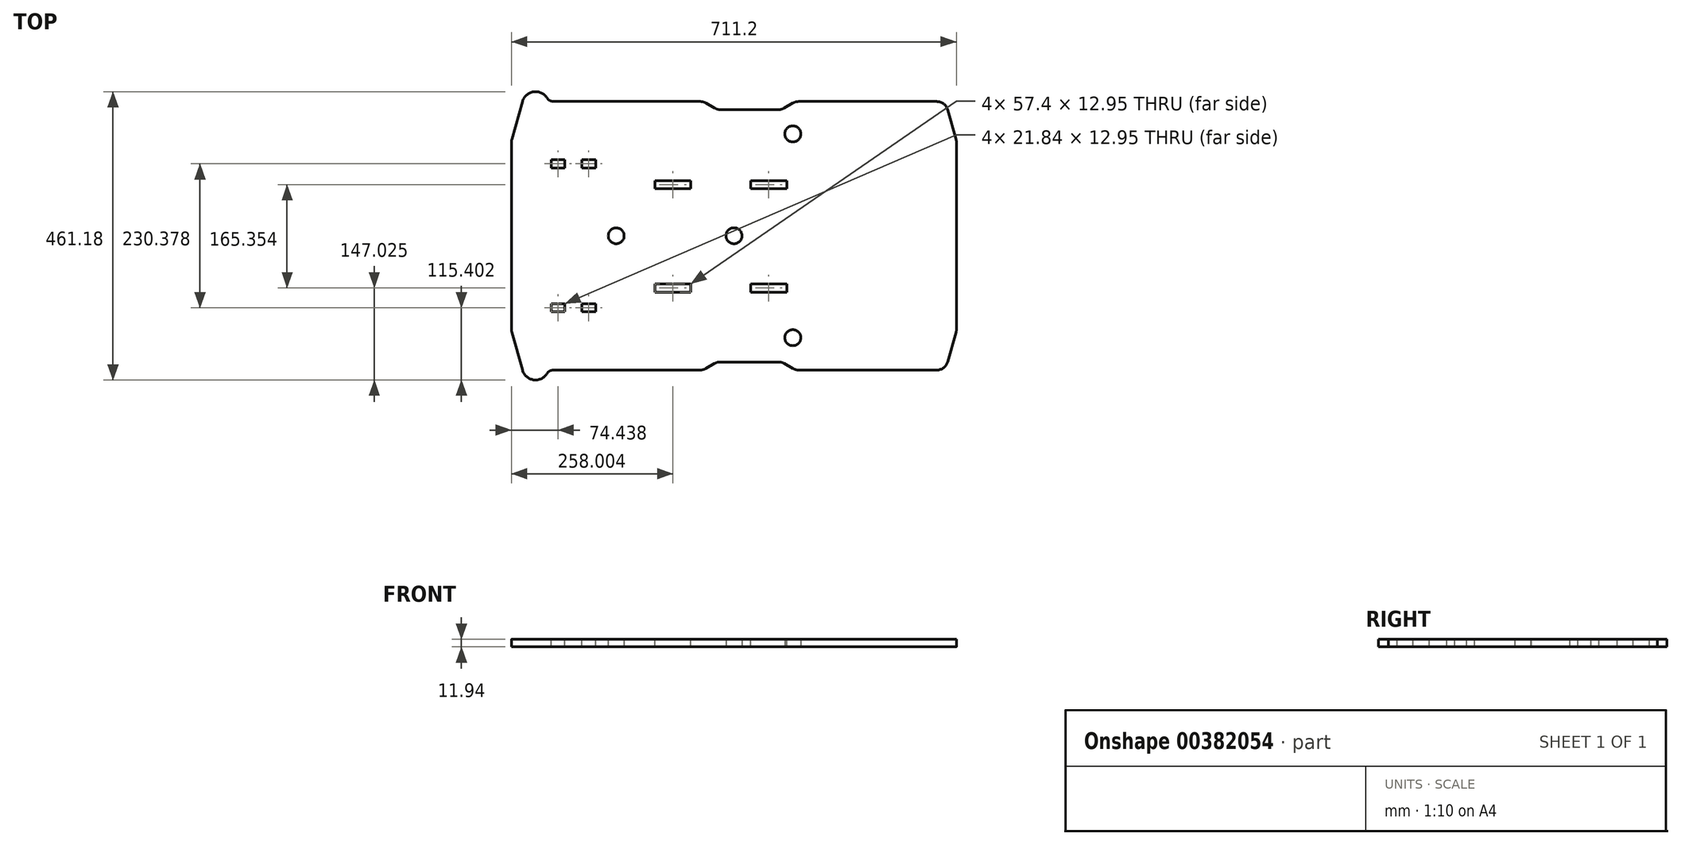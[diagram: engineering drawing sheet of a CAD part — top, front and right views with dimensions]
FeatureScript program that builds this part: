
annotation { "Feature Type Name" : "Feature", "Feature Type Description" : "" }
export const myFeature = defineFeature(function(context is Context, id is Id, definition is map)
    precondition{}
    {
        {
            var Q0;
            Q0=qCreatedBy(makeId("Top.planeOp"),FACE);
            var sketch = newSketch(context, id + "F0", { "sketchPlane" : qUnion([Q0])});
            skLineSegment(sketch, "E0.0", {"start": v(72.27, -53.52) * mm, "end": v(58.34, -61.56) * mm});
            skLineSegment(sketch, "E1.MirrorCS", {"start": v(72.27, 355.04) * mm, "end": v(58.34, 363.08) * mm});
            skLineSegment(sketch, "E2", {"start": v(81.54, -51.03) * mm, "end": v(174.21, -51.03) * mm});
            skLineSegment(sketch, "E3", {"start": v(81.54, 352.55) * mm, "end": v(174.21, 352.55) * mm});
            skLineSegment(sketch, "E4", {"start": v(49.07, 365.56) * mm, "end": v(-185.33, 365.56) * mm});
            skLineSegment(sketch, "E5", {"start": v(49.07, -64.04) * mm, "end": v(-185.33, -64.04) * mm});
            skArc(sketch, "E6", {"start": v(-234.87, -64.04) * mm, "mid": v(-217.19, -79.6) * mm, "end": v(-195.77, -69.78) * mm});
            skPoint(sketch, "E7.visualSharp", {"position": v(-193.21, -64.04) * mm});
            skArc(sketch, "E7.filletArc", {"start": v(-185.33, -64.04) * mm, "mid": v(-191.29, -65.57) * mm, "end": v(-195.77, -69.78) * mm});
            skLineSegment(sketch, "E8", {"start": v(-234.87, -64.04) * mm, "end": v(-251.8, -3.7) * mm});
            skArc(sketch, "E9.MirrorCS", {"start": v(-185.33, 365.56) * mm, "mid": v(-191.29, 367.1) * mm, "end": v(-195.77, 371.3) * mm});
            skArc(sketch, "E10.MirrorCS", {"start": v(-234.87, 365.56) * mm, "mid": v(-217.19, 381.12) * mm, "end": v(-195.77, 371.3) * mm});
            skLineSegment(sketch, "E11", {"start": v(-234.87, 365.56) * mm, "end": v(-251.8, 305.22) * mm});
            skLineSegment(sketch, "E12", {"start": v(-252.5, 19.7) * mm, "end": v(-252.5, 1.31) * mm});
            skLineSegment(sketch, "E13", {"start": v(-252.5, 281.82) * mm, "end": v(-252.5, 300.2) * mm});
            skPoint(sketch, "E14.visualSharp", {"position": v(-252.5, -1.24) * mm});
            skArc(sketch, "E14.filletArc", {"start": v(-252.5, 1.31) * mm, "mid": v(-252.32, -1.21) * mm, "end": v(-251.8, -3.7) * mm});
            skPoint(sketch, "E15.visualSharp", {"position": v(-252.5, 302.76) * mm});
            skArc(sketch, "E15.filletArc", {"start": v(-251.8, 305.22) * mm, "mid": v(-252.32, 302.74) * mm, "end": v(-252.5, 300.2) * mm});
            skLineSegment(sketch, "E16.MirrorCS", {"start": v(183.48, 355.04) * mm, "end": v(197.4, 363.08) * mm});
            skLineSegment(sketch, "E17.MirrorCS", {"start": v(183.48, -53.52) * mm, "end": v(197.4, -61.56) * mm});
            skLineSegment(sketch, "E18.MirrorCS", {"start": v(444.88, -50.5) * mm, "end": v(458.01, -3.7) * mm});
            skArc(sketch, "E19.MirrorCS", {"start": v(458.7, 1.31) * mm, "mid": v(458.53, -1.21) * mm, "end": v(458.01, -3.7) * mm});
            skLineSegment(sketch, "E20.MirrorCS", {"start": v(458.7, 19.7) * mm, "end": v(458.7, 1.31) * mm});
            skLineSegment(sketch, "E21.MirrorCS", {"start": v(458.7, 281.82) * mm, "end": v(458.7, 300.2) * mm});
            skArc(sketch, "E22.MirrorCS", {"start": v(458.01, 305.22) * mm, "mid": v(458.53, 302.74) * mm, "end": v(458.7, 300.2) * mm});
            skLineSegment(sketch, "E23.MirrorCS", {"start": v(444.88, 352.03) * mm, "end": v(458.01, 305.22) * mm});
            skLineSegment(sketch, "E24.MirrorCS", {"start": v(206.68, -64.04) * mm, "end": v(427.02, -64.04) * mm});
            skLineSegment(sketch, "E25.MirrorCS", {"start": v(206.68, 365.56) * mm, "end": v(427.02, 365.56) * mm});
            skPoint(sketch, "E26.visualSharp", {"position": v(441.08, 365.56) * mm});
            skArc(sketch, "E26.filletArc", {"start": v(444.88, 352.03) * mm, "mid": v(438.23, 361.8) * mm, "end": v(427.02, 365.56) * mm});
            skPoint(sketch, "E27.visualSharp", {"position": v(441.08, -64.04) * mm});
            skArc(sketch, "E27.filletArc", {"start": v(427.02, -64.04) * mm, "mid": v(438.23, -60.27) * mm, "end": v(444.88, -50.5) * mm});
            skPoint(sketch, "E28.visualSharp", {"position": v(54.04, -64.04) * mm});
            skArc(sketch, "E28.filletArc", {"start": v(49.07, -64.04) * mm, "mid": v(53.87, -63.4) * mm, "end": v(58.34, -61.56) * mm});
            skPoint(sketch, "E29.visualSharp", {"position": v(76.57, -51.03) * mm});
            skArc(sketch, "E29.filletArc", {"start": v(81.54, -51.03) * mm, "mid": v(76.74, -51.67) * mm, "end": v(72.27, -53.52) * mm});
            skPoint(sketch, "E30.visualSharp", {"position": v(179.18, -51.03) * mm});
            skArc(sketch, "E30.filletArc", {"start": v(183.48, -53.52) * mm, "mid": v(179.01, -51.67) * mm, "end": v(174.21, -51.03) * mm});
            skPoint(sketch, "E31.visualSharp", {"position": v(201.7, -64.04) * mm});
            skArc(sketch, "E31.filletArc", {"start": v(197.4, -61.56) * mm, "mid": v(201.88, -63.4) * mm, "end": v(206.68, -64.04) * mm});
            skPoint(sketch, "E32.visualSharp", {"position": v(179.18, 352.55) * mm});
            skArc(sketch, "E32.filletArc", {"start": v(174.21, 352.55) * mm, "mid": v(179.01, 353.19) * mm, "end": v(183.48, 355.04) * mm});
            skPoint(sketch, "E33.visualSharp", {"position": v(201.7, 365.56) * mm});
            skArc(sketch, "E33.filletArc", {"start": v(206.68, 365.56) * mm, "mid": v(201.88, 364.93) * mm, "end": v(197.4, 363.08) * mm});
            skPoint(sketch, "E34.visualSharp", {"position": v(76.57, 352.55) * mm});
            skArc(sketch, "E34.filletArc", {"start": v(72.27, 355.04) * mm, "mid": v(76.74, 353.19) * mm, "end": v(81.54, 352.55) * mm});
            skPoint(sketch, "E35.visualSharp", {"position": v(54.04, 365.56) * mm});
            skArc(sketch, "E35.filletArc", {"start": v(58.34, 363.08) * mm, "mid": v(53.87, 364.93) * mm, "end": v(49.07, 365.56) * mm});
            skLineSegment(sketch, "E36", {"start": v(-252.5, 281.82) * mm, "end": v(-252.5, 19.7) * mm});
            skLineSegment(sketch, "E37", {"start": v(458.7, 281.82) * mm, "end": v(458.7, 19.7) * mm});
            skCircle(sketch, "E38", {"center": v(103.1, 150.76) * mm, "radius": 12.83 * mm});
            skLineSegment(sketch, "E39", {"start": v(103.31, 163.59) * mm, "end": v(103.31, 352.55) * mm, "construction": true});
            skCircle(sketch, "E40", {"center": v(-85.09, 150.76) * mm, "radius": 12.7 * mm});
            skPoint(sketch, "E41", {"position": v(197.2, -12.22) * mm});
            skPoint(sketch, "E42", {"position": v(197.2, 313.74) * mm});
            skCircle(sketch, "E43", {"center": v(197.2, -12.22) * mm, "radius": 12.83 * mm});
            skCircle(sketch, "E44", {"center": v(197.2, 313.74) * mm, "radius": 12.83 * mm});
            skSolve(sketch);
        }
        {
            var Q0;
            Q0=makeQuery(id+"F0.imprint","IMPRINT",FACE,{"disambiguationData":[TD([[makeQuery(id+"F0.imprint","IMPRINT",EDGE,{"derivedFrom":sQuery(id+"F0.wireOp",EDGE,"E0.0")}),-1.0]])]});
            extrude(context, id + "F1", {"entities" : qUnion([Q0]), "depth" : 11.94 * mm});
        }
        {
            var Q0;
            Q0=makeQuery(id+"F1.opExtrude","CAP_FACE",FACE,{"disambiguationData":[OSD([sQuery(id+"F0.wireOp",EDGE,"E0.0"),sQuery(id+"F0.wireOp",EDGE,"E1.MirrorCS"),sQuery(id+"F0.wireOp",EDGE,"E2"),sQuery(id+"F0.wireOp",EDGE,"E3"),sQuery(id+"F0.wireOp",EDGE,"E4"),sQuery(id+"F0.wireOp",EDGE,"E5"),sQuery(id+"F0.wireOp",EDGE,"E6"),sQuery(id+"F0.wireOp",EDGE,"E7.filletArc"),sQuery(id+"F0.wireOp",EDGE,"E8"),sQuery(id+"F0.wireOp",EDGE,"E9.MirrorCS"),sQuery(id+"F0.wireOp",EDGE,"E10.MirrorCS"),sQuery(id+"F0.wireOp",EDGE,"E11"),sQuery(id+"F0.wireOp",EDGE,"E12"),sQuery(id+"F0.wireOp",EDGE,"E13"),sQuery(id+"F0.wireOp",EDGE,"E14.filletArc"),sQuery(id+"F0.wireOp",EDGE,"E15.filletArc"),sQuery(id+"F0.wireOp",EDGE,"E16.MirrorCS"),sQuery(id+"F0.wireOp",EDGE,"E17.MirrorCS"),sQuery(id+"F0.wireOp",EDGE,"E18.MirrorCS"),sQuery(id+"F0.wireOp",EDGE,"E19.MirrorCS"),sQuery(id+"F0.wireOp",EDGE,"E20.MirrorCS"),sQuery(id+"F0.wireOp",EDGE,"E21.MirrorCS"),sQuery(id+"F0.wireOp",EDGE,"E22.MirrorCS"),sQuery(id+"F0.wireOp",EDGE,"E23.MirrorCS"),sQuery(id+"F0.wireOp",EDGE,"E24.MirrorCS"),sQuery(id+"F0.wireOp",EDGE,"E25.MirrorCS"),sQuery(id+"F0.wireOp",EDGE,"E26.filletArc"),sQuery(id+"F0.wireOp",EDGE,"E27.filletArc"),sQuery(id+"F0.wireOp",EDGE,"E28.filletArc"),sQuery(id+"F0.wireOp",EDGE,"E29.filletArc"),sQuery(id+"F0.wireOp",EDGE,"E30.filletArc"),sQuery(id+"F0.wireOp",EDGE,"E31.filletArc"),sQuery(id+"F0.wireOp",EDGE,"E32.filletArc"),sQuery(id+"F0.wireOp",EDGE,"E33.filletArc"),sQuery(id+"F0.wireOp",EDGE,"E34.filletArc"),sQuery(id+"F0.wireOp",EDGE,"E35.filletArc"),sQuery(id+"F0.wireOp",EDGE,"E36"),sQuery(id+"F0.wireOp",EDGE,"E37"),sQuery(id+"F0.wireOp",EDGE,"E38"),sQuery(id+"F0.wireOp",EDGE,"E40"),sQuery(id+"F0.wireOp",EDGE,"E43"),sQuery(id+"F0.wireOp",EDGE,"E44")])],"isStart":false});
            var sketch = newSketch(context, id + "F2", { "sketchPlane" : qUnion([Q0])});
            skLineSegment(sketch, "E45", {"start": v(-185.8, 29.1) * mm, "end": v(-170.31, 29.1) * mm});
            skLineSegment(sketch, "E46", {"start": v(-185.8, 42.05) * mm, "end": v(-170.31, 42.05) * mm});
            skLineSegment(sketch, "E47", {"start": v(-170.31, 35.57) * mm, "end": v(-136.6, 35.57) * mm, "construction": true});
            skLineSegment(sketch, "E48", {"start": v(-153.46, 35.57) * mm, "end": v(-153.46, 41.61) * mm, "construction": true});
            skLineSegment(sketch, "E49.MirrorCS", {"start": v(-136.6, 29.1) * mm, "end": v(-136.6, 42.05) * mm, "construction": true});
            skLineSegment(sketch, "E50.MirrorCS", {"start": v(-121.11, 42.05) * mm, "end": v(-136.6, 42.05) * mm});
            skLineSegment(sketch, "E51.MirrorCS", {"start": v(-139.78, 35.57) * mm, "end": v(-170.31, 35.57) * mm, "construction": true});
            skLineSegment(sketch, "E52.MirrorCS", {"start": v(-121.11, 29.1) * mm, "end": v(-121.11, 42.05) * mm, "construction": true});
            skLineSegment(sketch, "E53.MirrorCS", {"start": v(-121.11, 29.1) * mm, "end": v(-136.6, 29.1) * mm});
            skLineSegment(sketch, "E54", {"start": v(-185.8, 42.05) * mm, "end": v(-185.8, 259.47) * mm, "construction": true});
            skLineSegment(sketch, "E55", {"start": v(-185.8, 150.76) * mm, "end": v(-157.57, 150.76) * mm, "construction": true});
            skLineSegment(sketch, "E56.MirrorCS", {"start": v(-170.31, 265.95) * mm, "end": v(-136.6, 265.95) * mm, "construction": true});
            skLineSegment(sketch, "E57.MirrorCS", {"start": v(-153.46, 265.95) * mm, "end": v(-153.46, 259.9) * mm, "construction": true});
            skLineSegment(sketch, "E58.MirrorCS", {"start": v(-121.11, 259.47) * mm, "end": v(-136.6, 259.47) * mm});
            skLineSegment(sketch, "E59.MirrorCS", {"start": v(-136.6, 265.95) * mm, "end": v(-170.31, 265.95) * mm, "construction": true});
            skLineSegment(sketch, "E60.MirrorCS", {"start": v(-185.8, 272.43) * mm, "end": v(-170.31, 272.43) * mm});
            skLineSegment(sketch, "E61.MirrorCS", {"start": v(-121.11, 272.43) * mm, "end": v(-136.6, 272.43) * mm});
            skLineSegment(sketch, "E62.MirrorCS", {"start": v(-185.8, 259.47) * mm, "end": v(-170.31, 259.47) * mm});
            skLineSegment(sketch, "E63", {"start": v(-178.06, 29.1) * mm, "end": v(-178.06, 42.05) * mm, "construction": true});
            skLineSegment(sketch, "E64", {"start": v(-128.86, 29.1) * mm, "end": v(-128.86, 42.05) * mm, "construction": true});
            skLineSegment(sketch, "E65", {"start": v(-121.11, 42.05) * mm, "end": v(-117.94, 42.05) * mm});
            skLineSegment(sketch, "E66", {"start": v(-117.94, 42.05) * mm, "end": v(-117.94, 29.1) * mm});
            skLineSegment(sketch, "E67", {"start": v(-121.11, 29.1) * mm, "end": v(-117.94, 29.1) * mm});
            skLineSegment(sketch, "E68.MirrorCS", {"start": v(-136.6, 42.05) * mm, "end": v(-139.78, 42.05) * mm});
            skLineSegment(sketch, "E69.MirrorCS", {"start": v(-139.78, 42.05) * mm, "end": v(-139.78, 29.1) * mm});
            skLineSegment(sketch, "E70.MirrorCS", {"start": v(-136.6, 29.1) * mm, "end": v(-139.78, 29.1) * mm});
            skPoint(sketch, "E71.orphan", {"position": v(-136.6, 35.57) * mm});
            skLineSegment(sketch, "E72", {"start": v(-170.31, 42.05) * mm, "end": v(-167.14, 42.05) * mm});
            skLineSegment(sketch, "E73", {"start": v(-167.14, 42.05) * mm, "end": v(-167.14, 29.1) * mm});
            skLineSegment(sketch, "E74", {"start": v(-170.31, 29.1) * mm, "end": v(-167.14, 29.1) * mm});
            skLineSegment(sketch, "E75.MirrorCS", {"start": v(-185.8, 42.05) * mm, "end": v(-188.98, 42.05) * mm});
            skLineSegment(sketch, "E76.MirrorCS", {"start": v(-188.98, 42.05) * mm, "end": v(-188.98, 29.1) * mm});
            skLineSegment(sketch, "E77.MirrorCS", {"start": v(-185.8, 29.1) * mm, "end": v(-188.98, 29.1) * mm});
            skPoint(sketch, "E78", {"position": v(-170.31, 42.05) * mm});
            skPoint(sketch, "E79", {"position": v(-170.31, 29.1) * mm});
            skLineSegment(sketch, "E80", {"start": v(-170.31, 29.1) * mm, "end": v(-170.31, 42.05) * mm, "construction": true});
            skPoint(sketch, "E81", {"position": v(-185.8, 42.05) * mm});
            skPoint(sketch, "E82", {"position": v(-185.8, 29.1) * mm});
            skLineSegment(sketch, "E83", {"start": v(-185.8, 29.1) * mm, "end": v(-185.8, 42.05) * mm, "construction": true});
            skLineSegment(sketch, "E84.MirrorCS", {"start": v(-185.8, 259.47) * mm, "end": v(-188.98, 259.47) * mm});
            skLineSegment(sketch, "E85.MirrorCS", {"start": v(-170.31, 272.43) * mm, "end": v(-167.14, 272.43) * mm});
            skLineSegment(sketch, "E86.MirrorCS", {"start": v(-170.31, 259.47) * mm, "end": v(-167.14, 259.47) * mm});
            skLineSegment(sketch, "E87.MirrorCS", {"start": v(-188.98, 259.47) * mm, "end": v(-188.98, 272.43) * mm});
            skLineSegment(sketch, "E88.MirrorCS", {"start": v(-167.14, 259.47) * mm, "end": v(-167.14, 272.43) * mm});
            skLineSegment(sketch, "E89.MirrorCS", {"start": v(-136.6, 272.43) * mm, "end": v(-139.78, 272.43) * mm});
            skLineSegment(sketch, "E90.MirrorCS", {"start": v(-185.8, 272.43) * mm, "end": v(-188.98, 272.43) * mm});
            skLineSegment(sketch, "E91.MirrorCS", {"start": v(-121.11, 259.47) * mm, "end": v(-117.94, 259.47) * mm});
            skLineSegment(sketch, "E92.MirrorCS", {"start": v(-117.94, 259.47) * mm, "end": v(-117.94, 272.43) * mm});
            skLineSegment(sketch, "E93.MirrorCS", {"start": v(-121.11, 272.43) * mm, "end": v(-117.94, 272.43) * mm});
            skLineSegment(sketch, "E94.MirrorCS", {"start": v(-136.6, 259.47) * mm, "end": v(-139.78, 259.47) * mm});
            skLineSegment(sketch, "E95.MirrorCS", {"start": v(-139.78, 259.47) * mm, "end": v(-139.78, 272.43) * mm});
            skLineSegment(sketch, "E96.MirrorCS", {"start": v(-178.06, 272.43) * mm, "end": v(-178.06, 259.47) * mm, "construction": true});
            skLineSegment(sketch, "E97.MirrorCS", {"start": v(-128.86, 272.43) * mm, "end": v(-128.86, 259.47) * mm, "construction": true});
            skLineSegment(sketch, "E98.MirrorCS", {"start": v(-139.78, 265.95) * mm, "end": v(-170.31, 265.95) * mm, "construction": true});
            skPoint(sketch, "E99.MirrorP", {"position": v(-170.31, 259.47) * mm});
            skPoint(sketch, "E100.MirrorP", {"position": v(-170.31, 272.43) * mm});
            skPoint(sketch, "E101.MirrorP", {"position": v(-185.8, 272.43) * mm});
            skPoint(sketch, "E102.MirrorP", {"position": v(-136.6, 265.95) * mm});
            skPoint(sketch, "E103.MirrorP", {"position": v(-185.8, 259.47) * mm});
            skLineSegment(sketch, "E104", {"start": v(-170.31, 259.47) * mm, "end": v(-170.31, 272.43) * mm, "construction": true});
            skLineSegment(sketch, "E105", {"start": v(-185.8, 259.47) * mm, "end": v(-185.8, 272.43) * mm, "construction": true});
            skPoint(sketch, "E106", {"position": v(-136.6, 272.43) * mm});
            skPoint(sketch, "E107", {"position": v(-121.11, 272.43) * mm});
            skPoint(sketch, "E108", {"position": v(-121.11, 259.47) * mm});
            skPoint(sketch, "E109", {"position": v(-136.6, 259.47) * mm});
            skLineSegment(sketch, "E110", {"start": v(-136.6, 259.47) * mm, "end": v(-136.6, 272.43) * mm, "construction": true});
            skLineSegment(sketch, "E111", {"start": v(-121.11, 272.43) * mm, "end": v(-121.11, 259.47) * mm, "construction": true});
            skSolve(sketch);
        }
        {
            var Q0;
            Q0=makeQuery(id+"F2.imprint","IMPRINT",FACE,{"disambiguationData":[TD([[makeQuery(id+"F2.imprint","IMPRINT",EDGE,{"derivedFrom":sQuery(id+"F2.wireOp",EDGE,"E84.MirrorCS")}),-1.0]])]});
            var Q1;
            Q1=makeQuery(id+"F2.imprint","IMPRINT",FACE,{"disambiguationData":[TD([[makeQuery(id+"F2.imprint","IMPRINT",EDGE,{"derivedFrom":sQuery(id+"F2.wireOp",EDGE,"E89.MirrorCS")}),1.0]])]});
            var Q2;
            Q2=makeQuery(id+"F2.imprint","IMPRINT",FACE,{"disambiguationData":[TD([[makeQuery(id+"F2.imprint","IMPRINT",EDGE,{"derivedFrom":sQuery(id+"F2.wireOp",EDGE,"E45")}),1.0]])]});
            var Q3;
            Q3=makeQuery(id+"F2.imprint","IMPRINT",FACE,{"disambiguationData":[TD([[makeQuery(id+"F2.imprint","IMPRINT",EDGE,{"derivedFrom":sQuery(id+"F2.wireOp",EDGE,"E50.MirrorCS")}),1.0]])]});
            extrude(context, id + "F3", {"entities" : qUnion([Q0, Q1, Q2, Q3]), "operationType" : NewBodyOperationType.REMOVE, "oppositeDirection" : true, "depth" : 25.4 * mm});
        }
        {
            var Q0;
            Q0=makeQuery(id+"F1.opExtrude","CAP_FACE",FACE,{"disambiguationData":[OSD([sQuery(id+"F0.wireOp",EDGE,"E0.0"),sQuery(id+"F0.wireOp",EDGE,"E1.MirrorCS"),sQuery(id+"F0.wireOp",EDGE,"E2"),sQuery(id+"F0.wireOp",EDGE,"E3"),sQuery(id+"F0.wireOp",EDGE,"E4"),sQuery(id+"F0.wireOp",EDGE,"E5"),sQuery(id+"F0.wireOp",EDGE,"E6"),sQuery(id+"F0.wireOp",EDGE,"E7.filletArc"),sQuery(id+"F0.wireOp",EDGE,"E8"),sQuery(id+"F0.wireOp",EDGE,"E9.MirrorCS"),sQuery(id+"F0.wireOp",EDGE,"E10.MirrorCS"),sQuery(id+"F0.wireOp",EDGE,"E11"),sQuery(id+"F0.wireOp",EDGE,"E12"),sQuery(id+"F0.wireOp",EDGE,"E13"),sQuery(id+"F0.wireOp",EDGE,"E14.filletArc"),sQuery(id+"F0.wireOp",EDGE,"E15.filletArc"),sQuery(id+"F0.wireOp",EDGE,"E16.MirrorCS"),sQuery(id+"F0.wireOp",EDGE,"E17.MirrorCS"),sQuery(id+"F0.wireOp",EDGE,"E18.MirrorCS"),sQuery(id+"F0.wireOp",EDGE,"E19.MirrorCS"),sQuery(id+"F0.wireOp",EDGE,"E20.MirrorCS"),sQuery(id+"F0.wireOp",EDGE,"E21.MirrorCS"),sQuery(id+"F0.wireOp",EDGE,"E22.MirrorCS"),sQuery(id+"F0.wireOp",EDGE,"E23.MirrorCS"),sQuery(id+"F0.wireOp",EDGE,"E24.MirrorCS"),sQuery(id+"F0.wireOp",EDGE,"E25.MirrorCS"),sQuery(id+"F0.wireOp",EDGE,"E26.filletArc"),sQuery(id+"F0.wireOp",EDGE,"E27.filletArc"),sQuery(id+"F0.wireOp",EDGE,"E28.filletArc"),sQuery(id+"F0.wireOp",EDGE,"E29.filletArc"),sQuery(id+"F0.wireOp",EDGE,"E30.filletArc"),sQuery(id+"F0.wireOp",EDGE,"E31.filletArc"),sQuery(id+"F0.wireOp",EDGE,"E32.filletArc"),sQuery(id+"F0.wireOp",EDGE,"E33.filletArc"),sQuery(id+"F0.wireOp",EDGE,"E34.filletArc"),sQuery(id+"F0.wireOp",EDGE,"E35.filletArc"),sQuery(id+"F0.wireOp",EDGE,"E36"),sQuery(id+"F0.wireOp",EDGE,"E37"),sQuery(id+"F0.wireOp",EDGE,"E38"),sQuery(id+"F0.wireOp",EDGE,"E40"),sQuery(id+"F0.wireOp",EDGE,"E43"),sQuery(id+"F0.wireOp",EDGE,"E44")])],"isStart":false});
            var sketch = newSketch(context, id + "F4", { "sketchPlane" : qUnion([Q0])});
            skLineSegment(sketch, "E112", {"start": v(-121.11, 41.16) * mm, "end": v(-121.11, 258.58) * mm, "construction": true});
            skLineSegment(sketch, "E113", {"start": v(-121.11, 149.87) * mm, "end": v(82.09, 149.87) * mm, "construction": true});
            skLineSegment(sketch, "E114", {"start": v(82.09, 149.87) * mm, "end": v(82.09, 226.07) * mm, "construction": true});
            skLineSegment(sketch, "E115.MirrorCS", {"start": v(82.09, 149.87) * mm, "end": v(82.09, 73.67) * mm, "construction": true});
            skPoint(sketch, "E116.MirrorCS.start.orphan", {"position": v(82.09, 73.67) * mm});
            skPoint(sketch, "E117.MirrorP", {"position": v(82.09, 226.07) * mm});
            skLineSegment(sketch, "E118", {"start": v(5.5, 60.72) * mm, "end": v(5.5, 73.67) * mm, "construction": true});
            skLineSegment(sketch, "E119", {"start": v(158.67, 60.72) * mm, "end": v(158.67, 73.67) * mm, "construction": true});
            skLineSegment(sketch, "E120", {"start": v(5.5, 226.07) * mm, "end": v(5.5, 239.03) * mm, "construction": true});
            skLineSegment(sketch, "E121", {"start": v(158.67, 226.07) * mm, "end": v(158.67, 239.03) * mm, "construction": true});
            skLineSegment(sketch, "E122", {"start": v(-20.02, 73.67) * mm, "end": v(-23.2, 73.67) * mm});
            skLineSegment(sketch, "E123", {"start": v(-20.02, 60.72) * mm, "end": v(-23.2, 60.72) * mm});
            skLineSegment(sketch, "E124", {"start": v(-23.2, 73.67) * mm, "end": v(-23.2, 60.72) * mm});
            skLineSegment(sketch, "E125.MirrorCS", {"start": v(31.03, 73.67) * mm, "end": v(34.2, 73.67) * mm});
            skLineSegment(sketch, "E126.MirrorCS", {"start": v(34.2, 73.67) * mm, "end": v(34.2, 60.72) * mm});
            skLineSegment(sketch, "E127.MirrorCS", {"start": v(31.03, 60.72) * mm, "end": v(34.2, 60.72) * mm});
            skPoint(sketch, "E128", {"position": v(-20.02, 73.67) * mm});
            skPoint(sketch, "E129", {"position": v(31.03, 73.67) * mm});
            skPoint(sketch, "E130", {"position": v(31.03, 60.72) * mm});
            skPoint(sketch, "E131", {"position": v(-20.02, 60.72) * mm});
            skLineSegment(sketch, "E132", {"start": v(-20.02, 73.67) * mm, "end": v(-20.02, 60.72) * mm, "construction": true});
            skLineSegment(sketch, "E133", {"start": v(31.03, 73.67) * mm, "end": v(31.03, 60.72) * mm, "construction": true});
            skLineSegment(sketch, "E134.MirrorCS", {"start": v(184.2, 73.67) * mm, "end": v(187.37, 73.67) * mm});
            skLineSegment(sketch, "E135.MirrorCS", {"start": v(133.14, 73.67) * mm, "end": v(129.96, 73.67) * mm});
            skLineSegment(sketch, "E136.MirrorCS", {"start": v(184.2, 60.72) * mm, "end": v(187.37, 60.72) * mm});
            skLineSegment(sketch, "E137.MirrorCS", {"start": v(133.14, 60.72) * mm, "end": v(129.96, 60.72) * mm});
            skPoint(sketch, "E138.MirrorP", {"position": v(184.2, 73.67) * mm});
            skLineSegment(sketch, "E139.MirrorCS", {"start": v(129.96, 73.67) * mm, "end": v(129.96, 60.72) * mm});
            skPoint(sketch, "E140.MirrorP", {"position": v(133.14, 73.67) * mm});
            skPoint(sketch, "E141.MirrorP", {"position": v(184.2, 60.72) * mm});
            skPoint(sketch, "E142.MirrorP", {"position": v(133.14, 60.72) * mm});
            skLineSegment(sketch, "E143.MirrorCS", {"start": v(187.37, 73.67) * mm, "end": v(187.37, 60.72) * mm});
            skLineSegment(sketch, "E144", {"start": v(184.2, 73.67) * mm, "end": v(184.2, 60.72) * mm, "construction": true});
            skLineSegment(sketch, "E145", {"start": v(133.14, 73.67) * mm, "end": v(133.14, 60.72) * mm, "construction": true});
            skLineSegment(sketch, "E146.MirrorCS", {"start": v(184.2, 226.07) * mm, "end": v(187.37, 226.07) * mm});
            skLineSegment(sketch, "E147.MirrorCS", {"start": v(133.14, 226.07) * mm, "end": v(129.96, 226.07) * mm});
            skLineSegment(sketch, "E148.MirrorCS", {"start": v(184.2, 239.03) * mm, "end": v(187.37, 239.03) * mm});
            skLineSegment(sketch, "E149.MirrorCS", {"start": v(133.14, 239.03) * mm, "end": v(129.96, 239.03) * mm});
            skLineSegment(sketch, "E150.MirrorCS", {"start": v(129.96, 226.07) * mm, "end": v(129.96, 239.03) * mm});
            skLineSegment(sketch, "E151.MirrorCS", {"start": v(-20.02, 226.07) * mm, "end": v(-23.2, 226.07) * mm});
            skLineSegment(sketch, "E152.MirrorCS", {"start": v(31.03, 226.07) * mm, "end": v(34.2, 226.07) * mm});
            skLineSegment(sketch, "E153.MirrorCS", {"start": v(187.37, 226.07) * mm, "end": v(187.37, 239.03) * mm});
            skLineSegment(sketch, "E154.MirrorCS", {"start": v(34.2, 226.07) * mm, "end": v(34.2, 239.03) * mm});
            skLineSegment(sketch, "E155.MirrorCS", {"start": v(31.03, 239.03) * mm, "end": v(34.2, 239.03) * mm});
            skLineSegment(sketch, "E156.MirrorCS", {"start": v(-23.2, 226.07) * mm, "end": v(-23.2, 239.03) * mm});
            skLineSegment(sketch, "E157.MirrorCS", {"start": v(-20.02, 239.03) * mm, "end": v(-23.2, 239.03) * mm});
            skLineSegment(sketch, "E158.MirrorCS", {"start": v(158.67, 239.03) * mm, "end": v(158.67, 226.07) * mm, "construction": true});
            skLineSegment(sketch, "E159.MirrorCS", {"start": v(5.5, 239.03) * mm, "end": v(5.5, 226.07) * mm, "construction": true});
            skPoint(sketch, "E160.MirrorP", {"position": v(31.03, 239.03) * mm});
            skPoint(sketch, "E161.MirrorP", {"position": v(133.14, 239.03) * mm});
            skPoint(sketch, "E162.MirrorP", {"position": v(184.2, 226.07) * mm});
            skPoint(sketch, "E163.MirrorP", {"position": v(31.03, 226.07) * mm});
            skPoint(sketch, "E164.MirrorP", {"position": v(-20.02, 239.03) * mm});
            skPoint(sketch, "E165.MirrorP", {"position": v(-20.02, 226.07) * mm});
            skPoint(sketch, "E166.MirrorP", {"position": v(133.14, 226.07) * mm});
            skPoint(sketch, "E167.MirrorP", {"position": v(184.2, 239.03) * mm});
            skLineSegment(sketch, "E168", {"start": v(31.03, 226.07) * mm, "end": v(31.03, 239.03) * mm, "construction": true});
            skLineSegment(sketch, "E169", {"start": v(-20.02, 239.03) * mm, "end": v(-20.02, 226.07) * mm, "construction": true});
            skLineSegment(sketch, "E170", {"start": v(133.14, 239.03) * mm, "end": v(133.14, 226.07) * mm, "construction": true});
            skLineSegment(sketch, "E171", {"start": v(184.2, 239.03) * mm, "end": v(184.2, 226.07) * mm, "construction": true});
            skLineSegment(sketch, "E172", {"start": v(-20.02, 239.03) * mm, "end": v(31.03, 239.03) * mm});
            skLineSegment(sketch, "E173", {"start": v(31.03, 226.07) * mm, "end": v(-20.02, 226.07) * mm});
            skLineSegment(sketch, "E174", {"start": v(133.14, 239.03) * mm, "end": v(184.2, 239.03) * mm});
            skLineSegment(sketch, "E175", {"start": v(184.2, 226.07) * mm, "end": v(133.14, 226.07) * mm});
            skLineSegment(sketch, "E176", {"start": v(133.14, 73.67) * mm, "end": v(184.2, 73.67) * mm});
            skLineSegment(sketch, "E177", {"start": v(184.2, 60.72) * mm, "end": v(133.14, 60.72) * mm});
            skLineSegment(sketch, "E178", {"start": v(31.03, 73.67) * mm, "end": v(-20.02, 73.67) * mm});
            skLineSegment(sketch, "E179", {"start": v(-20.02, 60.72) * mm, "end": v(31.03, 60.72) * mm});
            skSolve(sketch);
        }
        {
            var Q0;
            Q0=makeQuery(id+"F4.imprint","IMPRINT",FACE,{"disambiguationData":[TD([[makeQuery(id+"F4.imprint","IMPRINT",EDGE,{"derivedFrom":sQuery(id+"F4.wireOp",EDGE,"E122")}),1.0]])]});
            var Q1;
            Q1=makeQuery(id+"F4.imprint","IMPRINT",FACE,{"disambiguationData":[TD([[makeQuery(id+"F4.imprint","IMPRINT",EDGE,{"derivedFrom":sQuery(id+"F4.wireOp",EDGE,"E134.MirrorCS")}),-1.0]])]});
            var Q2;
            Q2=makeQuery(id+"F4.imprint","IMPRINT",FACE,{"disambiguationData":[TD([[makeQuery(id+"F4.imprint","IMPRINT",EDGE,{"derivedFrom":sQuery(id+"F4.wireOp",EDGE,"E151.MirrorCS")}),-1.0]])]});
            var Q3;
            Q3=makeQuery(id+"F4.imprint","IMPRINT",FACE,{"disambiguationData":[TD([[makeQuery(id+"F4.imprint","IMPRINT",EDGE,{"derivedFrom":sQuery(id+"F4.wireOp",EDGE,"E146.MirrorCS")}),1.0]])]});
            extrude(context, id + "F5", {"entities" : qUnion([Q0, Q1, Q2, Q3]), "operationType" : NewBodyOperationType.REMOVE, "oppositeDirection" : true, "depth" : 25.4 * mm});
        }
    });
